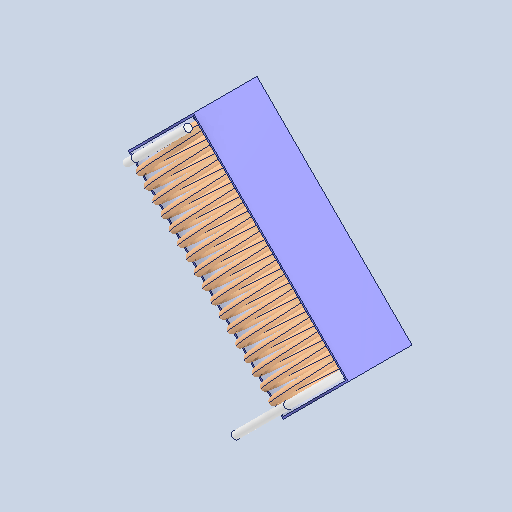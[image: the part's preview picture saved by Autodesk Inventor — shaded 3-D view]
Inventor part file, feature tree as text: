
AUTODESK INVENTOR PART (.ipt)
format: ipt  version: 2025 (Build 290162000, 162)  size: 712,704 bytes
history: native  units: mm
features: sweep x1, other x1
ambient origin geometry x8: Origin, YZ Plane, XZ Plane, XY Plane, X Axis, Y Axis, Z Axis, Center Point
bodies: Solid1 (feature_tree), Solid2 (feature_tree)
feature tree (2):
  sweep  "Sweep9"
  other  "Cut-Extrude1"
